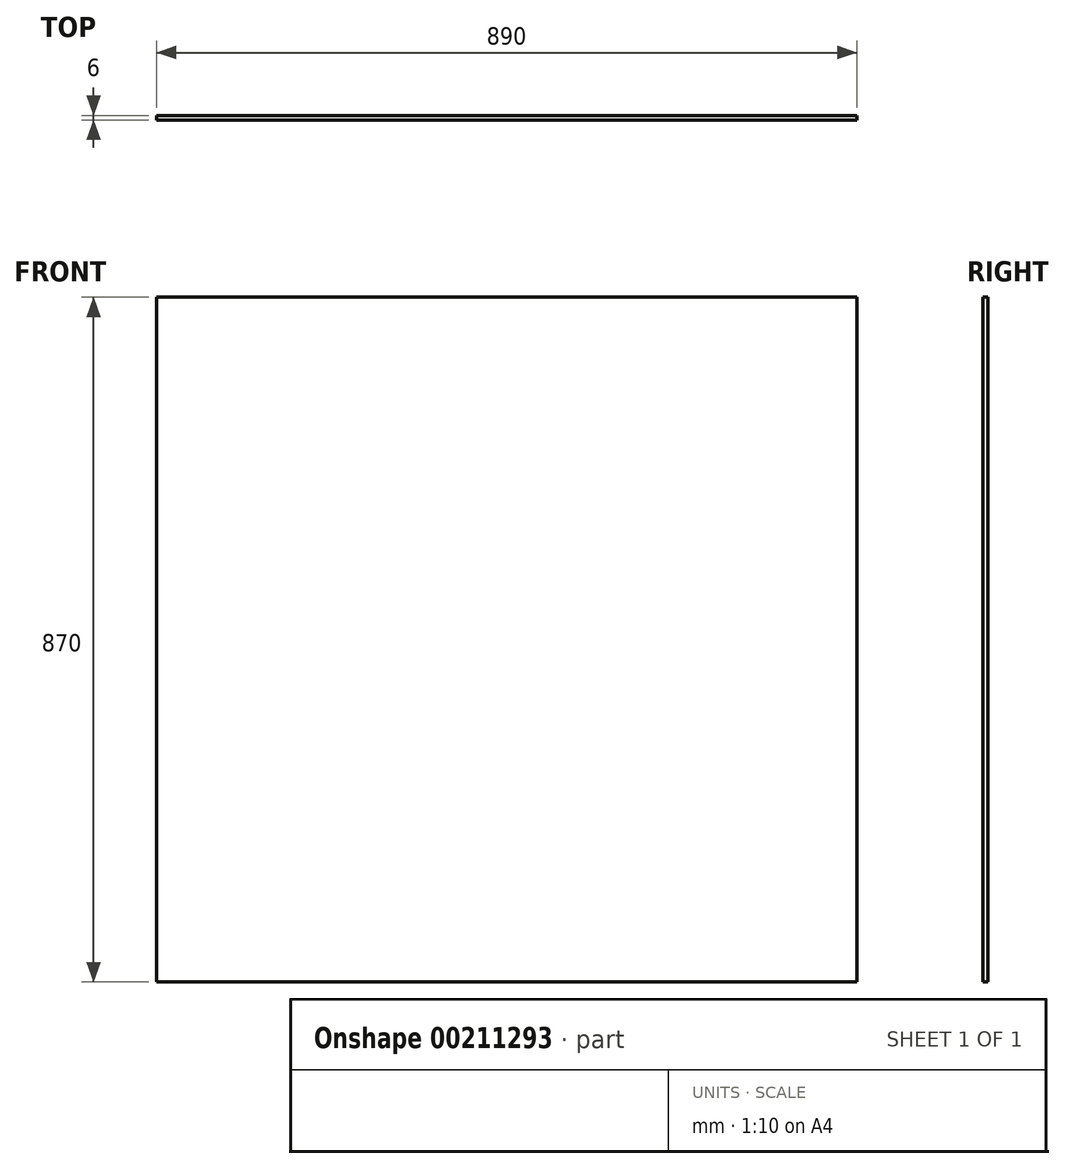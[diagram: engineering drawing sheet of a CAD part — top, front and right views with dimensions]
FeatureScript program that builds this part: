
annotation { "Feature Type Name" : "Feature", "Feature Type Description" : "" }
export const myFeature = defineFeature(function(context is Context, id is Id, definition is map)
    precondition{}
    {
        {
            var Q0;
            Q0=qCreatedBy(makeId("Front.planeOp"),FACE);
            var sketch = newSketch(context, id + "F0", { "sketchPlane" : qUnion([Q0])});
            skLineSegment(sketch, "E0.bottom", {"start": v(-445, 435) * mm, "end": v(445, 435) * mm});
            skLineSegment(sketch, "E0.top", {"start": v(-445, -435) * mm, "end": v(445, -435) * mm});
            skLineSegment(sketch, "E0.left", {"start": v(-445, 435) * mm, "end": v(-445, -435) * mm});
            skLineSegment(sketch, "E0.right", {"start": v(445, 435) * mm, "end": v(445, -435) * mm});
            skPoint(sketch, "E0.middle", {"position": v(0, 0) * mm});
            skSolve(sketch);
        }
        {
            var Q0;
            Q0=makeQuery(id+"F0.imprint","IMPRINT",FACE,{"disambiguationData":[TD([[makeQuery(id+"F0.imprint","IMPRINT",EDGE,{"derivedFrom":sQuery(id+"F0.wireOp",EDGE,"E0.bottom")}),-1.0]])]});
            extrude(context, id + "F1", {"entities" : qUnion([Q0]), "depth" : 6 * mm});
        }
    });
